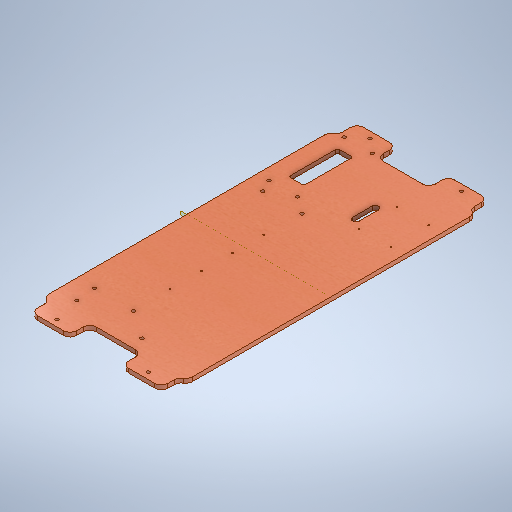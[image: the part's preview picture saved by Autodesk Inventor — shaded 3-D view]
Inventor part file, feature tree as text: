
AUTODESK INVENTOR PART (.ipt)
format: ipt  version: 2025.1 (Build 291241020, 241B)  size: 462,336 bytes
history: native  units: mm
features: sketch x10, reference x7, hole x6, other x6, extrude x4, plane x2, mirror x2, fillet x2, pattern_linear x1
ambient origin geometry x8: Origin, YZ Plane, XZ Plane, XY Plane, X Axis, Y Axis, Z Axis, Center Point
bodies: Solid1 (feature_tree)
feature tree (40):
  extrude  "Extrusion1"  Depth=220.0mm
  extrude  "Extrusion2"  Depth=5.0mm TaperAngle=0.0deg
  hole  "Hole1"  [1 undecoded]
  plane  "Work Plane1"
  plane  "Work Plane2"
  mirror  "Mirror1"
  mirror  "Mirror2"
  fillet  "Fillet1"  Radius=87.5mm
  hole  "Hole2"  [1 undecoded]
  pattern_linear  "Rectangular Pattern1"  Count1=5  [1 undecoded]
  hole  "Hole3"  [1 undecoded]
  hole  "Hole4"  [1 undecoded]
  hole  "Hole6"  [1 undecoded]
  hole  "Hole7"  [1 undecoded]
  extrude  "Extrusion4"  Depth=10.0mm
  fillet  "Fillet2"  Radius=48.0mm
  extrude  "Extrusion5"  Depth=10.0mm
  sketch  "Sketch1"  dims[d0=440.0mm d1=220.0mm]
  sketch  "Sketch2"  dims[d2=6.35mm d3=0.0mm d6=5.0mm d7=0.0mm]
  sketch  "Sketch3"  dims[d8=10.0mm]
  sketch  "Sketch4"  dims[d10=5.0mm d11=6.0mm d12=4.0mm d13=2.0mm d14=90.0deg d15=8.0mm d16=20.594885mm d17=10.0mm d18=87.5mm]
  sketch  "Sketch6"  dims[d19=132.075mm]
  sketch  "Sketch7"  dims[d20=5.0mm d21=6.0mm d22=4.0mm d23=2.0mm d24=90.0deg d25=8.0mm d26=20.594885mm d29=20.0mm d31=258.115mm d32=20.0mm d34=60.0mm]
  sketch  "Sketch9"  dims[d35=58.0mm]
  reference  "Reference4"
  reference  "Reference5"
  reference  "Reference6"
  sketch  "Sketch10"  dims[d36=49.0mm d37=50.0mm]
  reference  "Reference7"
  reference  "Reference8"
  reference  "Reference9"
  reference  "Reference10"
  sketch  "Sketch11"  dims[d38=20.0mm]
  sketch  "Sketch12"  dims[d39=2.1mm d40=6.0mm d41=4.0mm d42=2.0mm d43=90.0deg d44=6.0mm d45=0.0mm d46=100.0mm d49=5.0mm d50=6.0mm d51=10.0mm d52=2.5mm d53=90.0deg d54=8.0mm d55=20.594885mm d56=20.0mm d57=30.0mm d67=48.0mm d68=48.0mm d69=48.0mm d70=244.475mm d71=98.2375mm d72=20.0mm d73=2.6mm d74=6.0mm d75=4.0mm d76=2.0mm d77=90.0deg d78=10.0mm d79=0.0mm d80=30.0mm d81=60.0mm d82=10.0mm d83=30.0mm d84=5.0mm d85=6.0mm d86=4.0mm d87=2.0mm d88=90.0deg d89=8.0mm d90=20.594885mm d91=20.0mm d92=20.0mm d93=10.0mm d94=10.0mm d95=10.0mm d96=0.0mm d97=2.5mm d98=5.0mm d99=30.0mm d100=10.0mm d101=10.0mm d102=10.0mm d103=0.0mm]
  other  "MagDrop4.iam"
  other  "Connect4_LEG:1"
  other  "Connect4_LEG:2"
  other  "Connect4_RACK:1"
  other  "Control_Panel:1"
  other  "Control_Mount:1"
note: 7 required parameter values undecoded (feature->parameter linkage not recoverable at this tier; creation-order binding heuristic only, values carry confidence <= 0.55)
